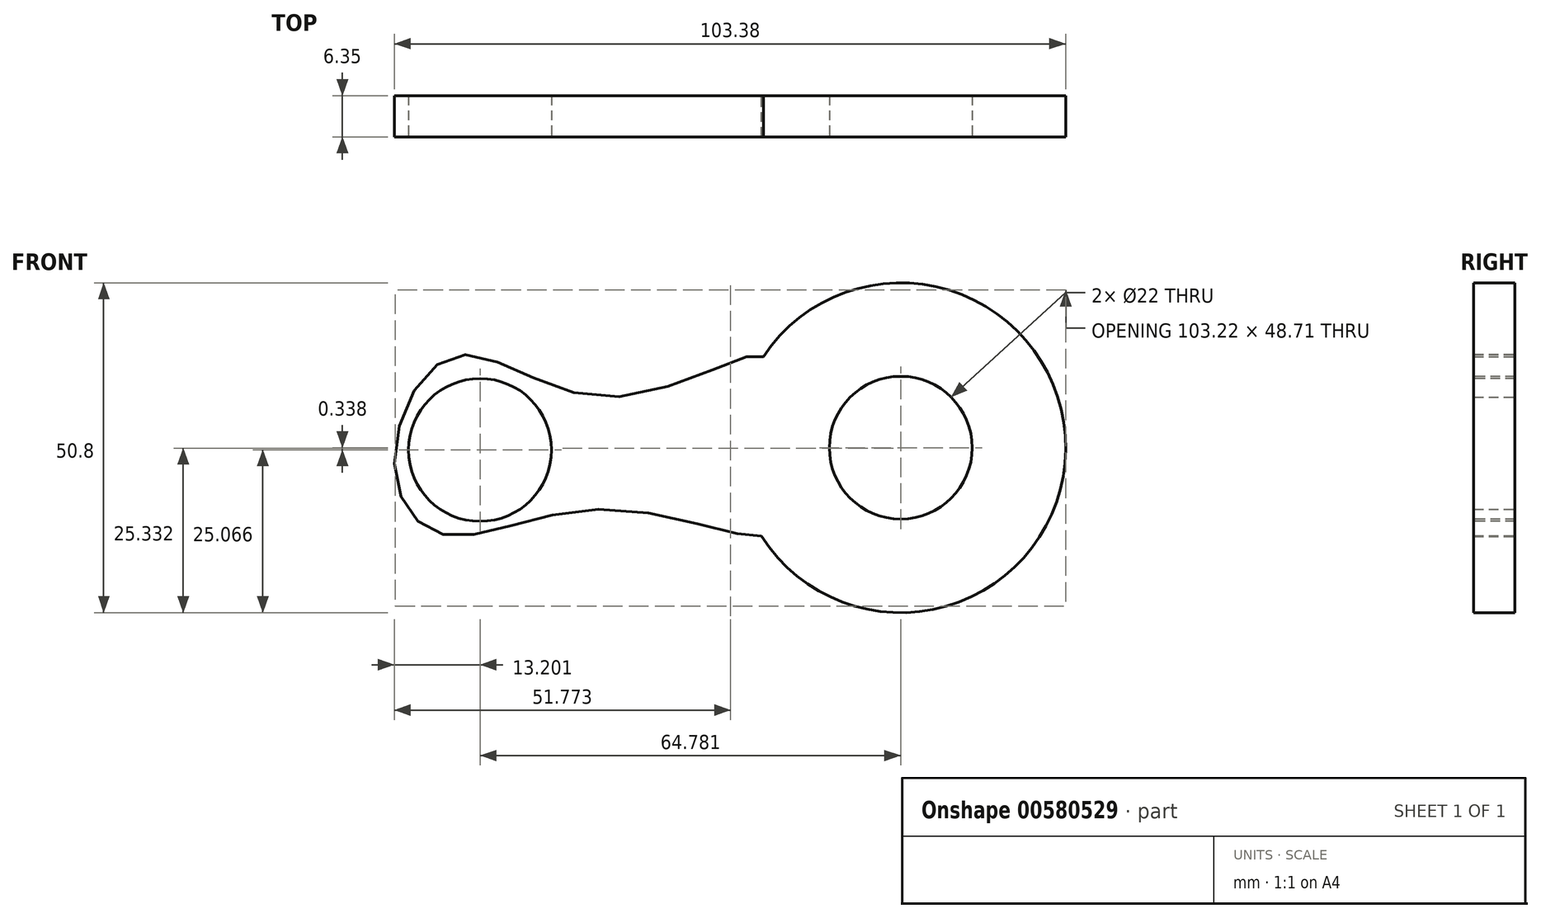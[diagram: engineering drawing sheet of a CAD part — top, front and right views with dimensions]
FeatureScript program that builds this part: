
annotation { "Feature Type Name" : "Feature", "Feature Type Description" : "" }
export const myFeature = defineFeature(function(context is Context, id is Id, definition is map)
    precondition{}
    {
        {
            var Q0;
            Q0=qCreatedBy(makeId("Front.planeOp"),FACE);
            var sketch = newSketch(context, id + "F0", { "sketchPlane" : qUnion([Q0])});
            skCircle(sketch, "E0", {"center": v(-31.23, 13.33) * mm, "radius": 25.4 * mm});
            skSolve(sketch);
        }
        {
            var Q0;
            Q0=makeQuery(id+"F0.imprint","IMPRINT",FACE,{"disambiguationData":[TD([[makeQuery(id+"F0.imprint","IMPRINT",EDGE,{"derivedFrom":sQuery(id+"F0.wireOp",EDGE,"E0")}),1.0]])]});
            var sketch = newSketch(context, id + "F1", { "sketchPlane" : qUnion([Q0])});
            skFitSpline(sketch, "E1", {"points": [v(-52.5, 27.51) * mm, v(-76.13, 21.1) * mm, v(-99.76, 27.51) * mm, v(-109.21, 11.3) * mm, v(-101.78, 0) * mm, v(-76.13, 3.88) * mm, v(-52.16, 0) * mm, v(-56.2, 12.66) * mm, v(-52.5, 27.51) * mm]});
            skSolve(sketch);
        }
        {
            var Q0;
            {var subQ0=sQuery(id+"F1.wireOp",EDGE,"E1");var subQ1=makeQuery(id+"F0.imprint","IMPRINT",EDGE,{"derivedFrom":sQuery(id+"F0.wireOp",EDGE,"E0")});var subQ2=makeQuery(id+"F1.imprint","INTERSECT",VERTEX,{"disambiguationData":[OD(0.0)],"derivedFrom":[subQ1,subQ0]});Q0=makeQuery(id+"F1.imprint","IMPRINT",FACE,{"disambiguationData":[TD([[makeQuery(id+"F1.imprint","IMPRINT",EDGE,{"disambiguationData":[TD([[subQ2,1.0]])],"derivedFrom":subQ0}),1.0]])]});}
            extrude(context, id + "F2", {"entities" : qUnion([Q0]), "depth" : 6.35 * mm, "offsetDistance" : 25.4 * mm});
        }
        {
            var Q0;
            Q0=makeQuery(id+"F0.imprint","IMPRINT",FACE,{"disambiguationData":[TD([[makeQuery(id+"F0.imprint","IMPRINT",EDGE,{"derivedFrom":sQuery(id+"F0.wireOp",EDGE,"E0")}),1.0]])]});
            extrude(context, id + "F3", {"entities" : qUnion([Q0]), "operationType" : NewBodyOperationType.ADD, "depth" : 6.35 * mm, "offsetDistance" : 25.4 * mm});
        }
        {
            var Q0;
            {var subQ0=sQuery(id+"F0.wireOp",EDGE,"E0");Q0=makeQuery(id+"Fh1F4jAGI78FEtO_1.boolean.opBoolean","MERGE",FACE,{"derivedFrom":[makeQuery(id+"F3.boolean.opBoolean","MERGE",FACE,{"derivedFrom":[makeQuery(id+"F2.opExtrude","CAP_FACE",FACE,{"disambiguationData":[OSD([subQ0,sQuery(id+"F1.wireOp",EDGE,"E1")])],"isStart":false}),makeQuery(id+"F3.opExtrude","CAP_FACE",FACE,{"disambiguationData":[OSD([subQ0])],"isStart":false})]}),makeQuery(id+"Fh1F4jAGI78FEtO_1.opExtrude","CAP_FACE",FACE,{"disambiguationData":[OSD([sQuery(id+"Fl5HFcsYkdjjjK5_1.wireOp",EDGE,"092b61e2-a2f5-43a3-b8e1-a7ad3c22eaaf")])],"isStart":false})]});}
            var sketch = newSketch(context, id + "F4", { "sketchPlane" : qUnion([Q0])});
            skCircle(sketch, "E2", {"center": v(-31.23, 13.33) * mm, "radius": 11 * mm});
            skSolve(sketch);
        }
        {
            var Q0;
            Q0=makeQuery(id+"F4.imprint","IMPRINT",FACE,{"disambiguationData":[TD([[makeQuery(id+"F4.imprint","IMPRINT",EDGE,{"derivedFrom":sQuery(id+"F4.wireOp",EDGE,"E2")}),1.0]])]});
            extrude(context, id + "F5", {"entities" : qUnion([Q0]), "operationType" : NewBodyOperationType.REMOVE, "oppositeDirection" : true, "depth" : 6.35 * mm, "offsetDistance" : 25.4 * mm});
        }
        {
            var Q0;
            {var subQ0=sQuery(id+"F0.wireOp",EDGE,"E0");Q0=makeQuery(id+"F3.boolean.opBoolean","MERGE",FACE,{"derivedFrom":[makeQuery(id+"F2.opExtrude","CAP_FACE",FACE,{"disambiguationData":[OSD([subQ0,sQuery(id+"F1.wireOp",EDGE,"E1")])],"isStart":false}),makeQuery(id+"F3.opExtrude","CAP_FACE",FACE,{"disambiguationData":[OSD([subQ0])],"isStart":false})]});}
            var sketch = newSketch(context, id + "F6", { "sketchPlane" : qUnion([Q0])});
            skCircle(sketch, "E3", {"center": v(-96, 13) * mm, "radius": 11 * mm});
            skSolve(sketch);
        }
        {
            var Q0;
            Q0=makeQuery(id+"F6.imprint","IMPRINT",FACE,{"disambiguationData":[TD([[makeQuery(id+"F6.imprint","IMPRINT",EDGE,{"derivedFrom":sQuery(id+"F6.wireOp",EDGE,"E3")}),1.0]])]});
            extrude(context, id + "F7", {"entities" : qUnion([Q0]), "operationType" : NewBodyOperationType.REMOVE, "oppositeDirection" : true, "depth" : 6.35 * mm, "offsetDistance" : 25.4 * mm});
        }
    });
